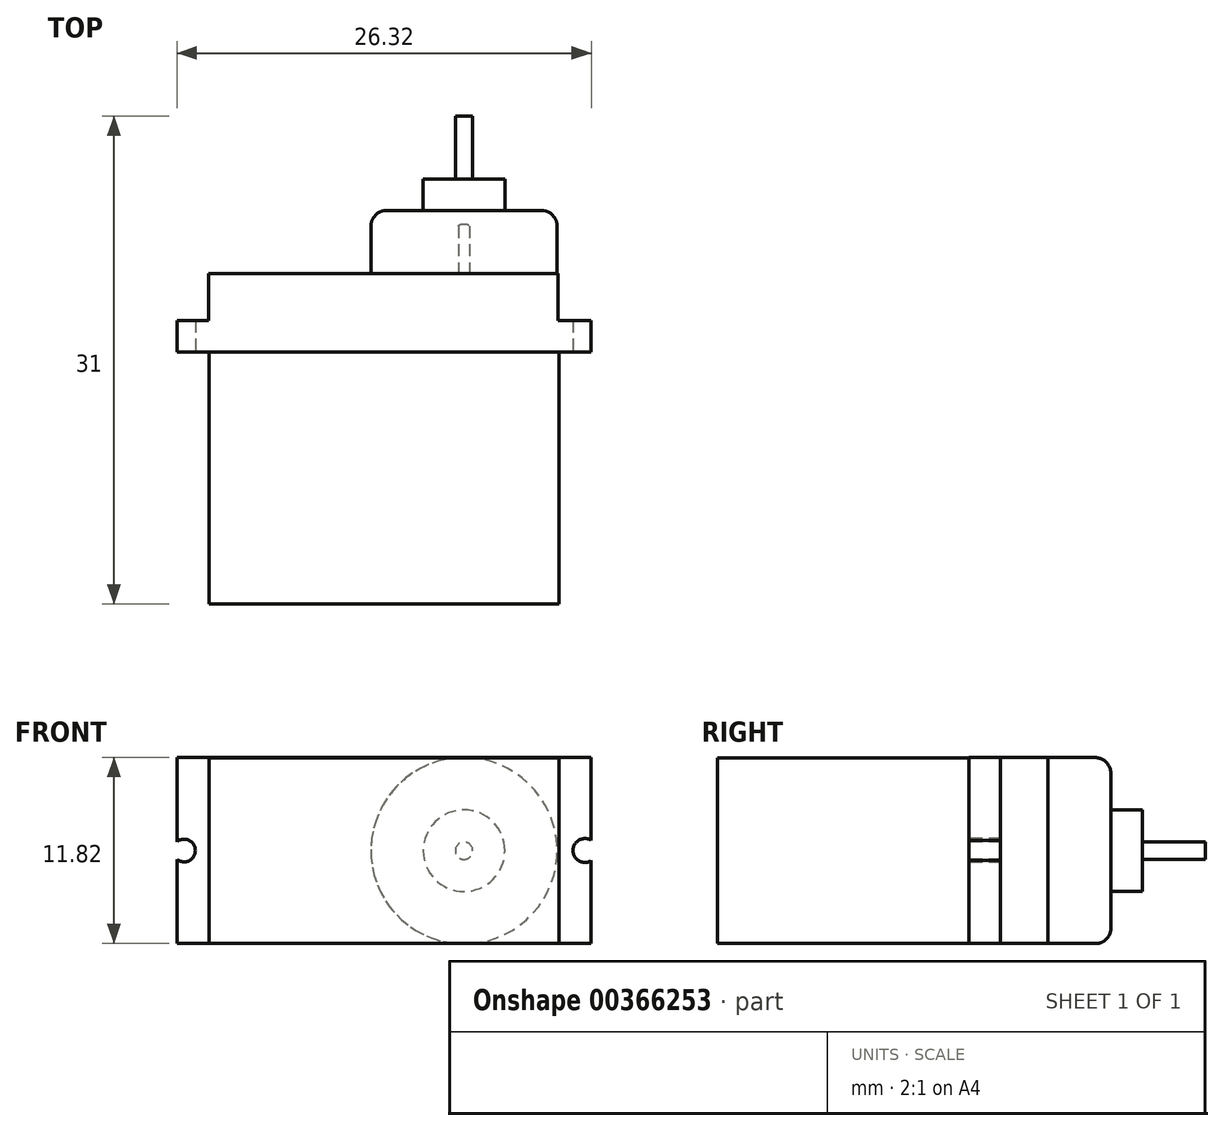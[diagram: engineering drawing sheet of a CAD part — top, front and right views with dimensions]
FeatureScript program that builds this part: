
annotation { "Feature Type Name" : "Feature", "Feature Type Description" : "" }
export const myFeature = defineFeature(function(context is Context, id is Id, definition is map)
    precondition{}
    {
        {
            var Q0;
            Q0=qCreatedBy(makeId("Front.planeOp"),FACE);
            var sketch = newSketch(context, id + "F0", { "sketchPlane" : qUnion([Q0])});
            skLineSegment(sketch, "E0.bottom", {"start": v(-64.03, 0) * mm, "end": v(-41.83, 0) * mm});
            skLineSegment(sketch, "E0.top", {"start": v(-64.03, 11.8) * mm, "end": v(-41.83, 11.8) * mm});
            skLineSegment(sketch, "E0.left", {"start": v(-64.03, 0) * mm, "end": v(-64.03, 11.8) * mm});
            skLineSegment(sketch, "E0.right", {"start": v(-41.83, 0) * mm, "end": v(-41.83, 11.8) * mm});
            skSolve(sketch);
        }
        {
            var Q0;
            Q0 = qSketchRegion(id + "F0", true);
            extrude(context, id + "F1", {"entities" : qUnion([Q0]), "depth" : 16 * mm});
        }
        {
            var Q0;
            Q0=qCreatedBy(makeId("Front.planeOp"),FACE);
            var sketch = newSketch(context, id + "F2", { "sketchPlane" : qUnion([Q0])});
            skLineSegment(sketch, "E1", {"start": v(-41.8, 11.82) * mm, "end": v(-39.77, 11.82) * mm});
            skLineSegment(sketch, "E2", {"start": v(-39.77, 0) * mm, "end": v(-41.83, 0) * mm});
            skLineSegment(sketch, "E3", {"start": v(-41.83, 0) * mm, "end": v(-64.03, 0) * mm});
            skLineSegment(sketch, "E4", {"start": v(-64.03, 0) * mm, "end": v(-66.09, 0) * mm});
            skLineSegment(sketch, "E5", {"start": v(-66.09, 11.82) * mm, "end": v(-64.03, 11.82) * mm});
            skLineSegment(sketch, "E6", {"start": v(-64.03, 11.82) * mm, "end": v(-41.8, 11.82) * mm});
            skLineSegment(sketch, "E7", {"start": v(-66.09, 0) * mm, "end": v(-66.09, 5.35) * mm});
            skLineSegment(sketch, "E8", {"start": v(-39.77, 0) * mm, "end": v(-39.77, 5.27) * mm});
            skArc(sketch, "E9", {"start": v(-66.09, 5.35) * mm, "mid": v(-64.91, 5.91) * mm, "end": v(-66.09, 6.47) * mm});
            skPoint(sketch, "E9.centerSnap0", {"position": v(-66.09, 5.91) * mm});
            skArc(sketch, "E10", {"start": v(-39.77, 6.55) * mm, "mid": v(-40.93, 5.91) * mm, "end": v(-39.77, 5.27) * mm});
            skPoint(sketch, "E10.centerSnap0", {"position": v(-39.77, 5.91) * mm});
            skLineSegment(sketch, "E11.trimOffspring", {"start": v(-66.09, 6.47) * mm, "end": v(-66.09, 11.82) * mm});
            skLineSegment(sketch, "E12.trimOffspring", {"start": v(-39.77, 6.55) * mm, "end": v(-39.77, 11.82) * mm});
            skSolve(sketch);
        }
        {
            var Q0;
            Q0 = qSketchRegion(id + "F2", true);
            extrude(context, id + "F3", {"entities" : qUnion([Q0]), "operationType" : NewBodyOperationType.ADD, "depth" : -2 * mm});
        }
        {
            var Q0;
            Q0=makeQuery(id+"F3.opExtrude","CAP_FACE",FACE,{"disambiguationData":[OSD([sQuery(id+"F2.wireOp",EDGE,"E1"),sQuery(id+"F2.wireOp",EDGE,"E2"),sQuery(id+"F2.wireOp",EDGE,"E3"),sQuery(id+"F2.wireOp",EDGE,"E4"),sQuery(id+"F2.wireOp",EDGE,"E5"),sQuery(id+"F2.wireOp",EDGE,"E6"),sQuery(id+"F2.wireOp",EDGE,"E7"),sQuery(id+"F2.wireOp",EDGE,"E8"),sQuery(id+"F2.wireOp",EDGE,"E9"),sQuery(id+"F2.wireOp",EDGE,"E10"),sQuery(id+"F2.wireOp",EDGE,"E11.trimOffspring"),sQuery(id+"F2.wireOp",EDGE,"E12.trimOffspring")])],"isStart":false});
            var sketch = newSketch(context, id + "F4", { "sketchPlane" : qUnion([Q0])});
            skLineSegment(sketch, "E13.bottom", {"start": v(41.88, 11.82) * mm, "end": v(64.08, 11.82) * mm});
            skLineSegment(sketch, "E13.top", {"start": v(41.88, 0) * mm, "end": v(64.08, 0) * mm});
            skLineSegment(sketch, "E13.left", {"start": v(41.88, 11.82) * mm, "end": v(41.88, 0) * mm});
            skLineSegment(sketch, "E13.right", {"start": v(64.08, 11.82) * mm, "end": v(64.08, 0) * mm});
            skSolve(sketch);
        }
        {
            var Q0;
            Q0 = qSketchRegion(id + "F4", true);
            extrude(context, id + "F5", {"entities" : qUnion([Q0]), "operationType" : NewBodyOperationType.ADD, "depth" : 3 * mm});
        }
        {
            var Q0;
            Q0=makeQuery(id+"F5.opExtrude","CAP_FACE",FACE,{"disambiguationData":[OSD([sQuery(id+"F4.wireOp",EDGE,"E13.bottom"),sQuery(id+"F4.wireOp",EDGE,"E13.top"),sQuery(id+"F4.wireOp",EDGE,"E13.left"),sQuery(id+"F4.wireOp",EDGE,"E13.right")])],"isStart":false});
            var sketch = newSketch(context, id + "F6", { "sketchPlane" : qUnion([Q0])});
            skCircle(sketch, "E14", {"center": v(47.85, 5.9) * mm, "radius": 5.91 * mm});
            skSolve(sketch);
        }
        {
            var Q0;
            {var subQ0=sQuery(id+"F6.wireOp",EDGE,"E14");var subQ1=makeQuery(id+"F5.opExtrude","CAP_EDGE",EDGE,{"disambiguationData":[OSD([sQuery(id+"F4.wireOp",EDGE,"E13.top")])],"isStart":false});var subQ2=makeQuery(id+"F6.imprint","INTERSECT",VERTEX,{"disambiguationData":[OD(0.0)],"derivedFrom":[subQ1,subQ0]});Q0=makeQuery(id+"F6.imprint","IMPRINT",FACE,{"disambiguationData":[TD([[makeQuery(id+"F6.imprint","IMPRINT",EDGE,{"disambiguationData":[TD([[subQ2,1.0]])],"derivedFrom":subQ0}),1.0]])]});}
            extrude(context, id + "F7", {"entities" : qUnion([Q0]), "operationType" : NewBodyOperationType.ADD, "depth" : 4 * mm});
        }
        {
            var Q0;
            Q0=makeQuery(id+"F7.opExtrude","CAP_EDGE",EDGE,{"disambiguationData":[OSD([sQuery(id+"F6.wireOp",EDGE,"E14")])],"isStart":false});
            fillet(context, id + "F8", {"entities" : qUnion([Q0]), "radius" : 1 * mm, "tangentPropagation" : true, "allowEdgeOverflow" : false});
        }
        {
            var Q0;
            Q0=makeQuery(id+"F7.opExtrude","CAP_FACE",FACE,{"disambiguationData":[OSD([sQuery(id+"F4.wireOp",EDGE,"E13.top"),sQuery(id+"F6.wireOp",EDGE,"E14")])],"isStart":false});
            var sketch = newSketch(context, id + "F9", { "sketchPlane" : qUnion([Q0])});
            skCircle(sketch, "E15", {"center": v(47.85, 5.9) * mm, "radius": 2.6 * mm});
            skSolve(sketch);
        }
        {
            var Q0;
            Q0 = qSketchRegion(id + "F9", true);
            extrude(context, id + "F10", {"entities" : qUnion([Q0]), "operationType" : NewBodyOperationType.ADD, "depth" : 2 * mm});
        }
        {
            var Q0;
            Q0=makeQuery(id+"F10.opExtrude","CAP_FACE",FACE,{"disambiguationData":[OSD([sQuery(id+"F9.wireOp",EDGE,"E15")])],"isStart":false});
            var sketch = newSketch(context, id + "F11", { "sketchPlane" : qUnion([Q0])});
            skCircle(sketch, "E16", {"center": v(47.85, 5.9) * mm, "radius": 0.55 * mm});
            skSolve(sketch);
        }
        {
            var Q0;
            Q0=makeQuery(id+"F11.imprint","IMPRINT",FACE,{"disambiguationData":[TD([[makeQuery(id+"F11.imprint","IMPRINT",EDGE,{"derivedFrom":sQuery(id+"F11.wireOp",EDGE,"E16")}),1.0]])]});
            extrude(context, id + "F12", {"entities" : qUnion([Q0]), "operationType" : NewBodyOperationType.ADD, "depth" : 4 * mm});
        }
        {
            var Q0;
            Q0=makeQuery(id+"F1.opExtrude","SWEPT_BODY",BODY,{"disambiguationData":[OSD([sQuery(id+"F0.wireOp",EDGE,"E0.bottom"),sQuery(id+"F0.wireOp",EDGE,"E0.top"),sQuery(id+"F0.wireOp",EDGE,"E0.left"),sQuery(id+"F0.wireOp",EDGE,"E0.right")])]});
            transform(context, id + "F13", {"entities" : qUnion([Q0]), "transformType" : TransformType.TRANSLATION_3D, "dx" : 0 * mm, "dy" : 0 * mm, "dz" : 0 * mm, "makeCopy" : true});
        }
    });
